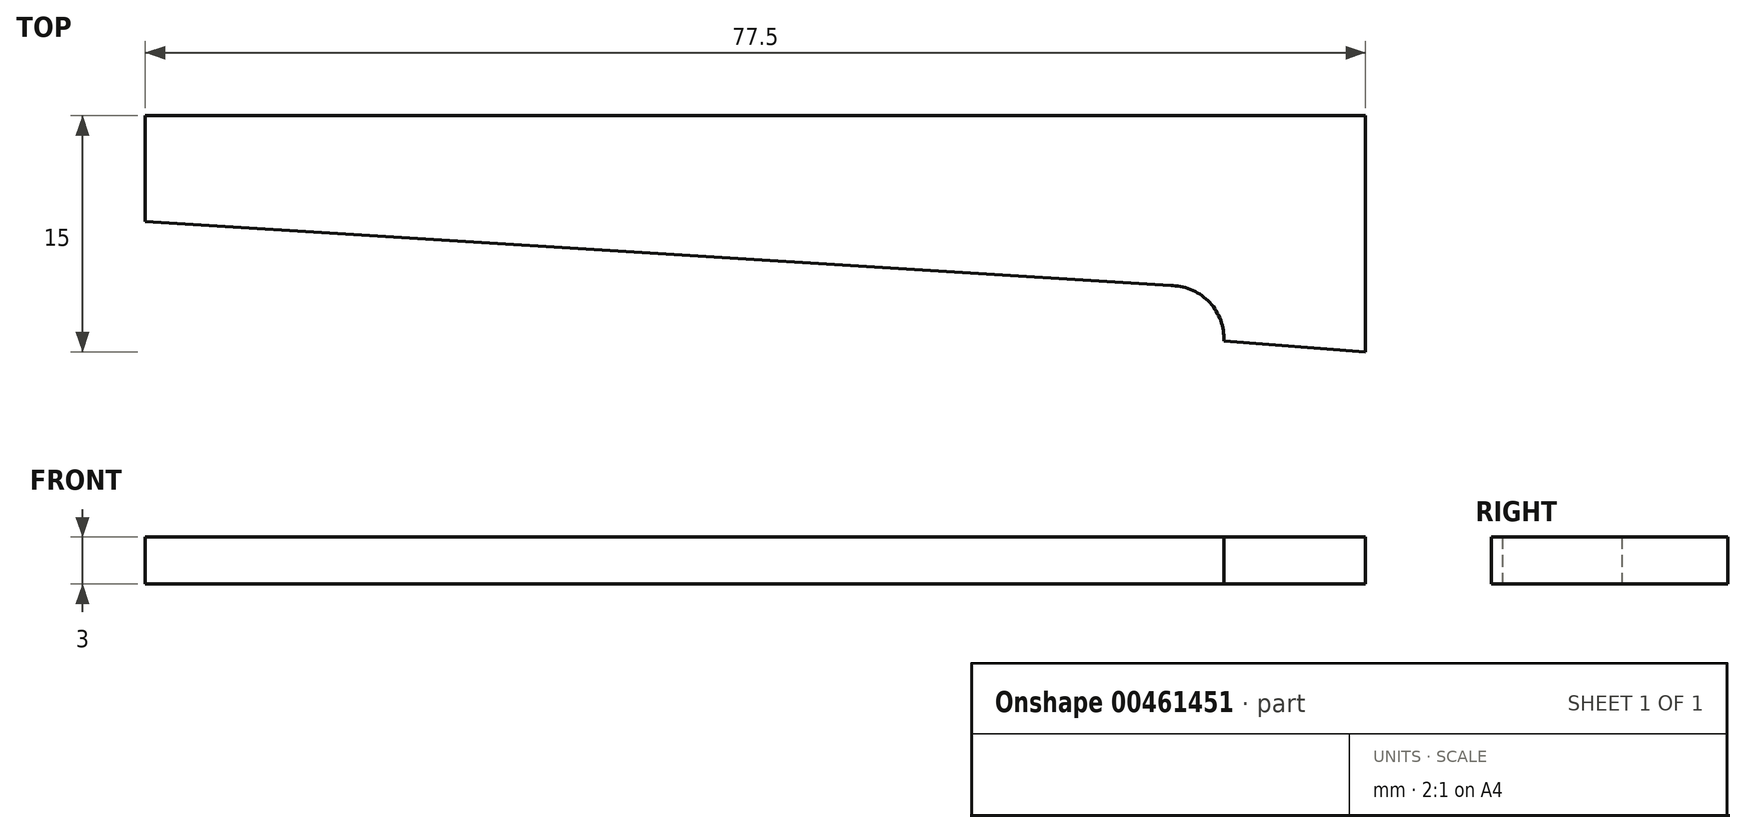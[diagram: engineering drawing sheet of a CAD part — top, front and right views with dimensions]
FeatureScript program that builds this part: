
annotation { "Feature Type Name" : "Feature", "Feature Type Description" : "" }
export const myFeature = defineFeature(function(context is Context, id is Id, definition is map)
    precondition{}
    {
        {
            var Q0;
            Q0=qCreatedBy(makeId("Top.planeOp"),FACE);
            var sketch = newSketch(context, id + "F0", { "sketchPlane" : qUnion([Q0])});
            skLineSegment(sketch, "E0.bottom", {"start": v(-32.5, 7.5) * mm, "end": v(32.5, 7.5) * mm});
            skLineSegment(sketch, "E0.top", {"start": v(-32.5, -7.5) * mm, "end": v(32.5, -7.5) * mm});
            skLineSegment(sketch, "E0.left", {"start": v(-32.5, 7.5) * mm, "end": v(-32.5, -7.5) * mm});
            skLineSegment(sketch, "E0.right", {"start": v(32.5, 7.5) * mm, "end": v(32.5, -7.5) * mm});
            skPoint(sketch, "E0.middle", {"position": v(0, 0) * mm});
            skPoint(sketch, "E1", {"position": v(23.5, -7.5) * mm});
            skPoint(sketch, "E2", {"position": v(-32.5, 0) * mm});
            skPoint(sketch, "E3", {"position": v(32.5, -3.5) * mm});
            skPoint(sketch, "E4", {"position": v(23.5, -3.5) * mm});
            skSolve(sketch);
        }
        {
            var Q0;
            Q0=makeQuery(id+"F0.imprint","IMPRINT",FACE,{"disambiguationData":[TD([[makeQuery(id+"F0.imprint","IMPRINT",EDGE,{"derivedFrom":sQuery(id+"F0.wireOp",EDGE,"E0.bottom")}),-1.0]])]});
            var sketch = newSketch(context, id + "F1", { "sketchPlane" : qUnion([Q0])});
            skLineSegment(sketch, "E5", {"start": v(-32.5, 0) * mm, "end": v(23.5, -3.5) * mm});
            skLineSegment(sketch, "E6", {"start": v(23.5, -3.5) * mm, "end": v(23.5, -7.5) * mm});
            skLineSegment(sketch, "E7", {"start": v(23.5, -6.8) * mm, "end": v(32.5, -7.5) * mm});
            skLineSegment(sketch, "E8", {"start": v(-45, 7.5) * mm, "end": v(32.5, 7.5) * mm});
            skLineSegment(sketch, "E9", {"start": v(32.5, 7.5) * mm, "end": v(32.5, -7.5) * mm});
            skArc(sketch, "E10", {"start": v(23.5, -6.8) * mm, "mid": v(22.59, -4.35) * mm, "end": v(20.2, -3.3) * mm});
            skLineSegment(sketch, "E11", {"start": v(-32.5, 0) * mm, "end": v(-45, 0.78) * mm});
            skLineSegment(sketch, "E12", {"start": v(-45, 7.5) * mm, "end": v(-45, 0.78) * mm});
            skSolve(sketch);
        }
        {
            var Q0;
            {var subQ0=sQuery(id+"F1.wireOp",EDGE,"E6");var subQ1=sQuery(id+"F1.wireOp",EDGE,"E5");var subQ2=makeQuery(id+"F1.imprint","INTERSECT",VERTEX,{"derivedFrom":[subQ1,subQ0]});Q0=makeQuery(id+"F1.imprint","IMPRINT",FACE,{"disambiguationData":[TD([[makeQuery(id+"F1.imprint","IMPRINT",EDGE,{"disambiguationData":[TD([[subQ2,1.0]])],"derivedFrom":subQ1}),-1.0]])]});}
            var Q1;
            {var subQ4=sQuery(id+"F1.wireOp",EDGE,"E7");Q1=makeQuery(id+"F1.imprint","IMPRINT",FACE,{"disambiguationData":[TD([[makeQuery(id+"F1.imprint","IMPRINT",EDGE,{"derivedFrom":subQ4}),1.0]])]});}
            var Q2;
            {var subQ4=sQuery(id+"F1.wireOp",EDGE,"E11");Q2=makeQuery(id+"F1.imprint","IMPRINT",FACE,{"disambiguationData":[TD([[makeQuery(id+"F1.imprint","IMPRINT",EDGE,{"derivedFrom":subQ4}),-1.0]])]});}
            extrude(context, id + "F2", {"entities" : qUnion([Q0, Q1, Q2]), "depth" : 3 * mm, "offsetDistance" : 25 * mm});
        }
        {
            var Q0;
            Q0=makeQuery(id+"F2.opExtrude","SWEPT_EDGE",EDGE,{"disambiguationData":[OSD([sQuery(id+"F0.wireOp",EDGE,"E0.left"),sQuery(id+"F1.wireOp",EDGE,"E5"),sQuery(id+"F1.wireOp",EDGE,"cPpSwtKI-4wKn-Qz6L-wNYk-TC8kZeUMuxxb")])]});
            fillet(context, id + "F3", {"entities" : qUnion([Q0]), "tangentPropagation" : true, "radius" : 4 * mm, "defaultsChanged" : true, "vertexSettings" : [], "allowEdgeOverflow" : false});
        }
    });
